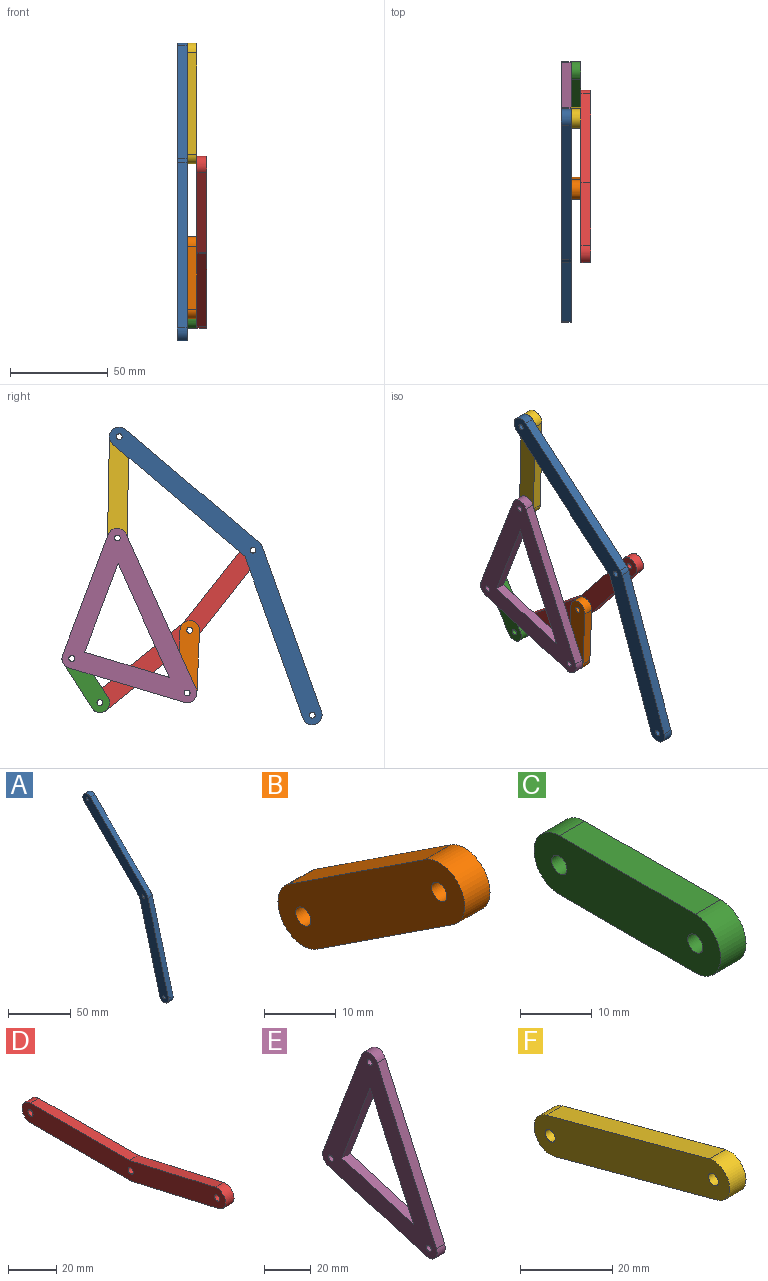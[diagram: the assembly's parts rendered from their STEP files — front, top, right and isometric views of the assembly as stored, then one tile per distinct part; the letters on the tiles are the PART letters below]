
ASSEMBLY  parts=6 mates=7
PART A: 12 faces, bbox 5x96.6x160 mm
  f0: plane 85.31x22.85mm, normal (0,0.97,-0.26), area 441.6mm2, adj f1,f7,f10,f11
  f1: plane 62.45x62.45mm, normal (0,0.71,-0.71), area 441.6mm2, adj f0,f2,f10,f11
  f2: cylinder r=5mm len=8.54mm, axis (-1,0,0), area 78.5mm2, adj f1,f3,f10,f11
  f3: plane 63.4x63.4mm, normal (0,-0.71,0.71), area 448.3mm2, adj f2,f4,f10,f11
  f4: cylinder r=5mm len=5mm, axis (-1,0,0), area 13.1mm2, adj f3,f5,f10,f11
  f5: plane 86.6x23.2mm, normal (0,-0.97,0.26), area 448.3mm2, adj f4,f7,f10,f11
  f6: cylinder r=1.5mm len=5mm, axis (-1,0,0), area 47.1mm2, adj f10,f11
  f7: cylinder r=5mm len=9.83mm, axis (-1,0,0), area 78.5mm2, adj f0,f5,f10,f11
  f8: cylinder r=1.5mm len=5mm, axis (-1,0,0), area 47.1mm2, adj f10,f11
  f9: cylinder r=1.5mm len=5mm, axis (-1,0,0), area 47.1mm2, adj f10,f11
  f10: plane 160x96.6mm, normal (1,0,0), area 1850.3mm2, adj f0,f1,f2,f3,f4,f5,f6,f7
  f11: plane 160x96.6mm, normal (-1,0,0), area 1850.3mm2, adj f0,f1,f2,f3,f4,f5,f6,f7
PART B: 8 faces, bbox 5x36.8x27.6 mm
  f0: cylinder r=5mm len=9.18mm, axis (-1,0,0), area 78.5mm2, adj f1,f5,f6,f7
  f1: plane 26.8x17.6mm, normal (0,-0.55,-0.84), area 160.3mm2, adj f0,f2,f6,f7
  f2: cylinder r=5mm len=9.18mm, axis (-1,0,0), area 78.5mm2, adj f1,f5,f6,f7
  f3: cylinder r=1.5mm len=5mm, axis (-1,0,0), area 47.1mm2, adj f6,f7
  f4: cylinder r=1.5mm len=5mm, axis (-1,0,0), area 47.1mm2, adj f6,f7
  f5: plane 26.8x17.6mm, normal (0,0.55,0.84), area 160.3mm2, adj f0,f2,f6,f7
  f6: plane 36.8x27.6mm, normal (1,0,0), area 385mm2, adj f0,f1,f2,f3,f4,f5
  f7: plane 36.8x27.6mm, normal (-1,0,0), area 385mm2, adj f0,f1,f2,f3,f4,f5
PART C: 8 faces, bbox 5x36.8x10 mm
  f0: cylinder r=5mm len=10mm, axis (-1,0,0), area 78.5mm2, adj f1,f5,f6,f7
  f1: plane 26.8x5mm, normal (0,0,1), area 134mm2, adj f0,f2,f6,f7
  f2: cylinder r=5mm len=10mm, axis (-1,0,0), area 78.5mm2, adj f1,f5,f6,f7
  f3: cylinder r=1.5mm len=5mm, axis (-1,0,0), area 47.1mm2, adj f6,f7
  f4: cylinder r=1.5mm len=5mm, axis (-1,0,0), area 47.1mm2, adj f6,f7
  f5: plane 26.8x5mm, normal (0,0,-1), area 134mm2, adj f0,f2,f6,f7
  f6: plane 36.8x10mm, normal (1,0,0), area 332.4mm2, adj f0,f1,f2,f3,f4,f5
  f7: plane 36.8x10mm, normal (-1,0,0), area 332.4mm2, adj f0,f1,f2,f3,f4,f5
PART D: 12 faces, bbox 5x119.9x21.6 mm
  f0: plane 58.44x5mm, normal (0,0,1), area 292.2mm2, adj f1,f7,f10,f11
  f1: plane 50.35x11.48mm, normal (0,0.22,0.98), area 258.2mm2, adj f0,f2,f10,f11
  f2: cylinder r=5mm len=9.88mm, axis (-1,0,0), area 78.5mm2, adj f1,f3,f10,f11
  f3: plane 50.9x11.6mm, normal (0,-0.22,-0.98), area 261mm2, adj f2,f4,f10,f11
  f4: cylinder r=5mm len=5mm, axis (-1,0,0), area 5.6mm2, adj f3,f5,f10,f11
  f5: plane 59x5mm, normal (0,0,-1), area 295mm2, adj f4,f7,f10,f11
  f6: cylinder r=1.5mm len=5mm, axis (-1,0,0), area 47.1mm2, adj f10,f11
  f7: cylinder r=5mm len=10mm, axis (-1,0,0), area 78.5mm2, adj f0,f5,f10,f11
  f8: cylinder r=1.5mm len=5mm, axis (-1,0,0), area 47.1mm2, adj f10,f11
  f9: cylinder r=1.5mm len=5mm, axis (-1,0,0), area 47.1mm2, adj f10,f11
  f10: plane 119.9x21.6mm, normal (1,0,0), area 1169.4mm2, adj f0,f1,f2,f3,f4,f5,f6,f7
  f11: plane 119.9x21.6mm, normal (-1,0,0), area 1169.4mm2, adj f0,f1,f2,f3,f4,f5,f6,f7
PART E: 14 faces, bbox 5x69x89.2 mm
  f0: plane 43.37x12.94mm, normal (0,-0.29,0.96), area 226.3mm2, adj f1,f9,f12,f13
  f1: plane 58.22x26.24mm, normal (0,0.91,-0.41), area 319.3mm2, adj f0,f9,f12,f13
  f2: cylinder r=5mm len=9.24mm, axis (-1,0,0), area 58.9mm2, adj f3,f10,f12,f13
  f3: plane 79.2x35.7mm, normal (0,-0.91,0.41), area 434.4mm2, adj f2,f4,f12,f13
  f4: cylinder r=5mm len=7.05mm, axis (-1,0,0), area 57.1mm2, adj f3,f5,f12,f13
  f5: plane 59x17.6mm, normal (0,0.29,-0.96), area 307.8mm2, adj f4,f6,f12,f13
  f6: cylinder r=5mm len=6.56mm, axis (-1,0,0), area 41.1mm2, adj f5,f10,f12,f13
  f7: cylinder r=1.5mm len=5mm, axis (-1,0,0), area 47.1mm2, adj f12,f13
  f8: cylinder r=1.5mm len=5mm, axis (-1,0,0), area 47.1mm2, adj f12,f13
  f9: plane 45.28x17.13mm, normal (0,-0.94,-0.35), area 242.1mm2, adj f0,f1,f12,f13
  f10: plane 61.6x23.3mm, normal (0,0.94,0.35), area 329.3mm2, adj f2,f6,f12,f13
  f11: cylinder r=1.5mm len=5mm, axis (-1,0,0), area 47.1mm2, adj f12,f13
  f12: plane 89.2x69mm, normal (1,0,0), area 2058.4mm2, adj f0,f1,f2,f3,f4,f5,f6,f7
  f13: plane 89.2x69mm, normal (-1,0,0), area 2058.4mm2, adj f0,f1,f2,f3,f4,f5,f6,f7
PART F: 8 faces, bbox 5x60x23.4 mm
  f0: cylinder r=5mm len=9.83mm, axis (-1,0,0), area 78.5mm2, adj f1,f5,f6,f7
  f1: plane 50x13.4mm, normal (0,0.26,0.97), area 258.8mm2, adj f0,f2,f6,f7
  f2: cylinder r=5mm len=9.83mm, axis (-1,0,0), area 78.5mm2, adj f1,f5,f6,f7
  f3: cylinder r=1.5mm len=5mm, axis (-1,0,0), area 47.1mm2, adj f6,f7
  f4: cylinder r=1.5mm len=5mm, axis (-1,0,0), area 47.1mm2, adj f6,f7
  f5: plane 50x13.4mm, normal (0,-0.26,-0.97), area 258.8mm2, adj f0,f2,f6,f7
  f6: plane 60x23.4mm, normal (1,0,0), area 582mm2, adj f0,f1,f2,f3,f4,f5
  f7: plane 60x23.4mm, normal (-1,0,0), area 582mm2, adj f0,f1,f2,f3,f4,f5
PLACE A rot(axis=(-1,0,0),4.7deg) t=(-89.8,36.93,46.02)mm
PLACE B rot(axis=(-1,0,0),54.3deg) t=(-84.8,-4.59,105.85)mm
PLACE C rot(axis=(1,0,0),57.5deg) t=(-84.8,137.14,-100.14)mm
PLACE D rot(axis=(-1,0,0),38.9deg) t=(-79.8,-5.21,77.55)mm
PLACE E t=(-89.8,0,0)mm fixed
PLACE F rot(axis=(-1,0,0),73.9deg) t=(-84.8,-32.49,230.03)mm
MATE revolute F.f2 <-> A.f2  axis (-1,0,0) through (-84.8,135.63,188.36)mm
MATE revolute E.f4 <-> B.f2  axis (1,0,0) through (-84.8,100.9,57.4)mm
MATE revolute B.f0 <-> D.f4  axis (1,0,0) through (-79.8,99.55,89.43)mm
MATE revolute E.f6 <-> C.f0  axis (1,0,0) through (-84.8,159.9,75)mm
MATE cylindrical D.f2 <-> A.f4  axis (-1,0,0) through (-79.8,67.21,130.41)mm
MATE revolute C.f2 <-> D.f6  axis (1,0,0) through (-79.8,145.49,52.41)mm
MATE revolute E.f2 <-> F.f0  axis (1,0,0) through (-84.8,136.6,136.6)mm
